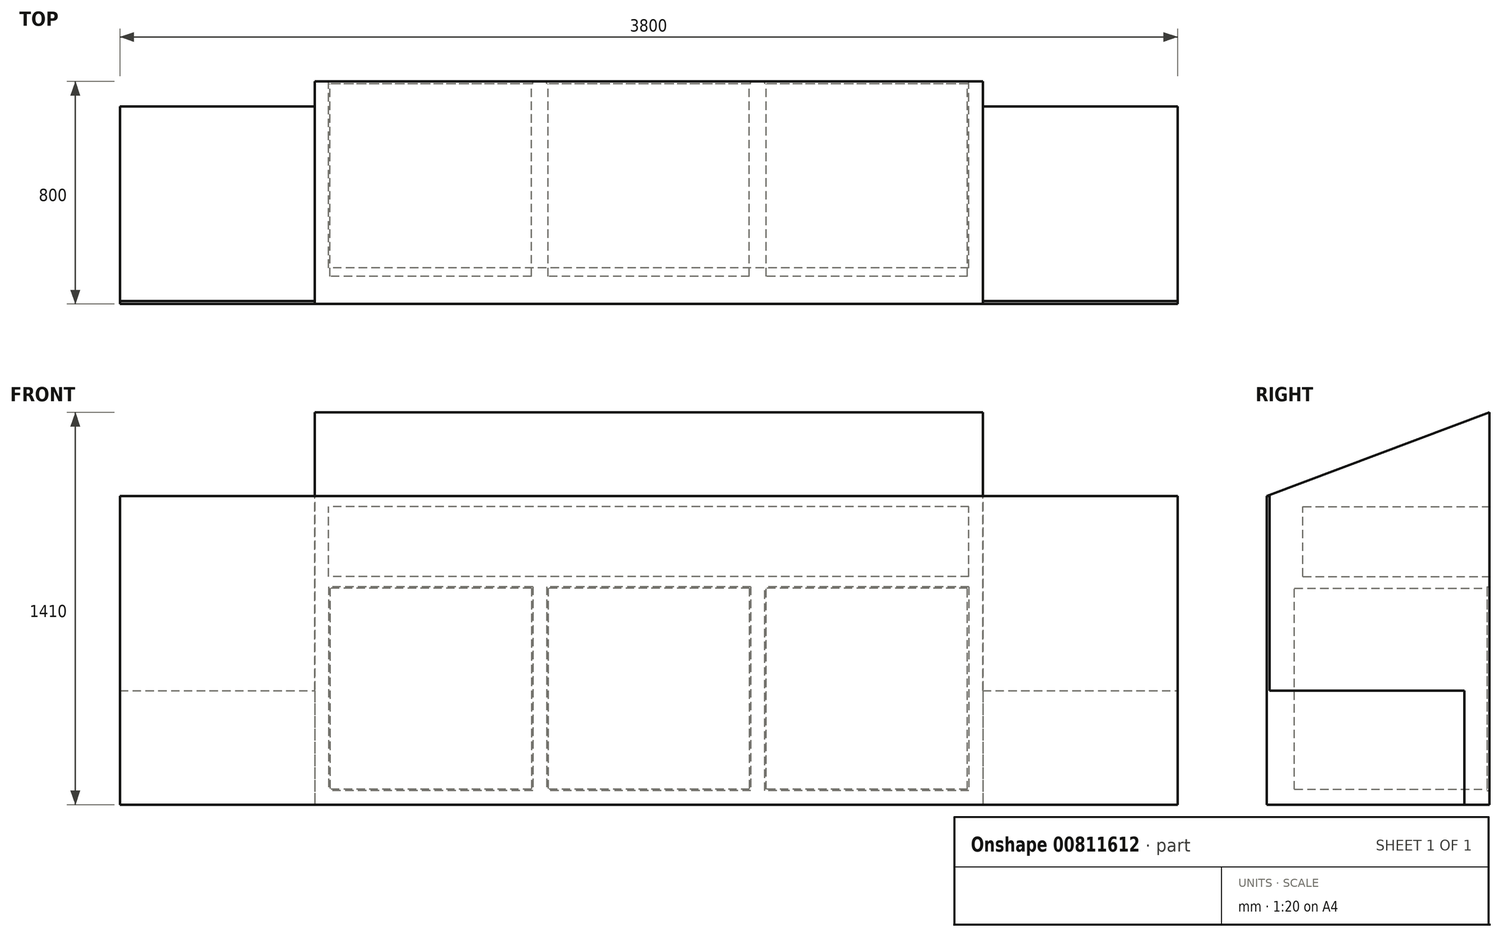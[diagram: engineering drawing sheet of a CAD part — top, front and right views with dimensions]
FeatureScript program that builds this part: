
annotation { "Feature Type Name" : "Feature", "Feature Type Description" : "" }
export const myFeature = defineFeature(function(context is Context, id is Id, definition is map)
    precondition{}
    {
        {
            var Q0;
            Q0=qCreatedBy(makeId("Top.planeOp"),FACE);
            var sketch = newSketch(context, id + "F0", { "sketchPlane" : qUnion([Q0])});
            skLineSegment(sketch, "E0.bottom", {"start": v(-1194.9, 289.22) * mm, "end": v(1205.1, 289.22) * mm});
            skLineSegment(sketch, "E0.top", {"start": v(-1194.9, -510.78) * mm, "end": v(1205.1, -510.78) * mm});
            skLineSegment(sketch, "E0.left", {"start": v(-1194.9, 289.22) * mm, "end": v(-1194.9, -510.78) * mm});
            skLineSegment(sketch, "E0.right", {"start": v(1205.1, 289.22) * mm, "end": v(1205.1, -510.78) * mm});
            skSolve(sketch);
        }
        {
            var Q0;
            Q0=makeQuery(id+"F0.imprint","IMPRINT",FACE,{"disambiguationData":[TD([[makeQuery(id+"F0.imprint","IMPRINT",EDGE,{"derivedFrom":sQuery(id+"F0.wireOp",EDGE,"E0.bottom")}),-1.0]])]});
            extrude(context, id + "F1", {"entities" : qUnion([Q0]), "depth" : 1110 * mm, "offsetDistance" : 25 * mm});
        }
        {
            var Q0;
            Q0=makeQuery(id+"F1.opExtrude","SWEPT_FACE",FACE,{"disambiguationData":[OSD([sQuery(id+"F0.wireOp",EDGE,"E0.top")])]});
            var sketch = newSketch(context, id + "F2", { "sketchPlane" : qUnion([Q0])});
            skLineSegment(sketch, "E1.bottom", {"start": v(-1194.9, 0) * mm, "end": v(-1894.9, 0) * mm});
            skLineSegment(sketch, "E1.top", {"start": v(-1194.9, 410) * mm, "end": v(-1894.9, 410) * mm});
            skLineSegment(sketch, "E1.left", {"start": v(-1194.9, 0) * mm, "end": v(-1194.9, 410) * mm});
            skLineSegment(sketch, "E1.right", {"start": v(-1894.9, 0) * mm, "end": v(-1894.9, 410) * mm});
            skLineSegment(sketch, "E2.bottom", {"start": v(1205.1, 0) * mm, "end": v(1905.1, 0) * mm});
            skLineSegment(sketch, "E2.top", {"start": v(1205.1, 410) * mm, "end": v(1905.1, 410) * mm});
            skLineSegment(sketch, "E2.left", {"start": v(1205.1, 0) * mm, "end": v(1205.1, 410) * mm});
            skLineSegment(sketch, "E2.right", {"start": v(1905.1, 0) * mm, "end": v(1905.1, 410) * mm});
            skSolve(sketch);
        }
        {
            var Q0;
            Q0 = qSketchRegion(id + "F2", true);
            extrude(context, id + "F3", {"entities" : qUnion([Q0]), "operationType" : NewBodyOperationType.ADD, "oppositeDirection" : true, "depth" : 710 * mm, "offsetDistance" : 25 * mm});
        }
        {
            var Q0;
            Q0=makeQuery(id+"F3.opExtrude","SWEPT_FACE",FACE,{"disambiguationData":[OSD([sQuery(id+"F2.wireOp",EDGE,"E2.top")])]});
            var sketch = newSketch(context, id + "F4", { "sketchPlane" : qUnion([Q0])});
            skLineSegment(sketch, "E3.0", {"start": v(-1894.9, 199.22) * mm, "end": v(-1894.9, -510.78) * mm});
            skLineSegment(sketch, "E4.bottom", {"start": v(-1894.9, -510.78) * mm, "end": v(1905.1, -510.78) * mm});
            skLineSegment(sketch, "E4.top", {"start": v(-1894.9, -500.78) * mm, "end": v(1905.1, -500.78) * mm});
            skLineSegment(sketch, "E4.left", {"start": v(-1894.9, -510.78) * mm, "end": v(-1894.9, -500.78) * mm});
            skLineSegment(sketch, "E4.right", {"start": v(1905.1, -510.78) * mm, "end": v(1905.1, -500.78) * mm});
            skSolve(sketch);
        }
        {
            var Q0;
            Q0 = qSketchRegion(id + "F4", true);
            extrude(context, id + "F5", {"entities" : qUnion([Q0]), "operationType" : NewBodyOperationType.ADD, "depth" : 700 * mm, "offsetDistance" : 25 * mm});
        }
        {
            var Q0;
            Q0=makeQuery(id+"F1.opExtrude","SWEPT_FACE",FACE,{"disambiguationData":[OSD([sQuery(id+"F0.wireOp",EDGE,"E0.left")])]});
            var sketch = newSketch(context, id + "F6", { "sketchPlane" : qUnion([Q0])});
            skLineSegment(sketch, "E5", {"start": v(-289.22, 1110) * mm, "end": v(-289.22, 1410) * mm});
            skLineSegment(sketch, "E6.0", {"start": v(-289.22, 1110) * mm, "end": v(500.78, 1110) * mm});
            skLineSegment(sketch, "E7", {"start": v(500.78, 1110) * mm, "end": v(510.78, 1110) * mm});
            skLineSegment(sketch, "E8", {"start": v(510.78, 1110) * mm, "end": v(-289.22, 1410) * mm});
            skSolve(sketch);
        }
        {
            var Q0;
            Q0=makeQuery(id+"F6.imprint","IMPRINT",FACE,{"disambiguationData":[TD([[makeQuery(id+"F6.imprint","IMPRINT",EDGE,{"derivedFrom":sQuery(id+"F6.wireOp",EDGE,"E5")}),-1.0]])]});
            var Q1;
            Q1=makeQuery(id+"F1.opExtrude","SWEPT_FACE",FACE,{"disambiguationData":[OSD([sQuery(id+"F0.wireOp",EDGE,"E0.right")])]});
            extrude(context, id + "F7", {"entities" : qUnion([Q0]), "operationType" : NewBodyOperationType.ADD, "endBound" : BoundingType.UP_TO_SURFACE, "oppositeDirection" : true, "depth" : 25 * mm, "endBoundEntityFace" : qUnion([Q1]), "offsetDistance" : 25 * mm});
        }
        {
            var Q0;
            Q0=makeQuery(id+"F7.boolean.opBoolean","MERGE",FACE,{"derivedFrom":[makeQuery(id+"F1.opExtrude","SWEPT_FACE",FACE,{"disambiguationData":[OSD([sQuery(id+"F0.wireOp",EDGE,"E0.bottom")])]}),makeQuery(id+"F7.opExtrude","SWEPT_FACE",FACE,{"disambiguationData":[OSD([sQuery(id+"F6.wireOp",EDGE,"E5")])]})]});
            var sketch = newSketch(context, id + "F8", { "sketchPlane" : qUnion([Q0])});
            skLineSegment(sketch, "E9.1", {"start": v(-1155.1, 783.3) * mm, "end": v(-1155.1, 50) * mm});
            skPoint(sketch, "E10.start.orphan", {"position": v(-1205.1, 1410) * mm});
            skPoint(sketch, "E11.end.orphan", {"position": v(1194.9, 1410) * mm});
            skLineSegment(sketch, "E12.top", {"start": v(-1155.1, 783.3) * mm, "end": v(-421.8, 783.3) * mm});
            skLineSegment(sketch, "E12.left", {"start": v(-1155.1, 50) * mm, "end": v(-1155.1, 783.3) * mm});
            skLineSegment(sketch, "E12.right", {"start": v(-421.8, 50) * mm, "end": v(-421.8, 783.3) * mm});
            skLineSegment(sketch, "E13.bottom", {"start": v(-371.8, 783.3) * mm, "end": v(361.5, 783.3) * mm});
            skLineSegment(sketch, "E13.top", {"start": v(-371.8, 50) * mm, "end": v(361.5, 50) * mm});
            skLineSegment(sketch, "E13.left", {"start": v(-371.8, 783.3) * mm, "end": v(-371.8, 50) * mm});
            skLineSegment(sketch, "E13.right", {"start": v(361.5, 783.3) * mm, "end": v(361.5, 50) * mm});
            skLineSegment(sketch, "E14.bottom", {"start": v(411.5, 783.3) * mm, "end": v(1144.8, 783.3) * mm});
            skLineSegment(sketch, "E14.top", {"start": v(411.5, 50) * mm, "end": v(1144.8, 50) * mm});
            skLineSegment(sketch, "E14.right", {"start": v(1144.8, 783.3) * mm, "end": v(1144.8, 50) * mm});
            skLineSegment(sketch, "E15.trimOffspring", {"start": v(1144.8, 50) * mm, "end": v(1144.9, 50) * mm});
            skPoint(sketch, "E16.end.orphan", {"position": v(-371.8, 627.14) * mm});
            skPoint(sketch, "E17.end.orphan", {"position": v(411.5, 495.55) * mm});
            skLineSegment(sketch, "E18", {"start": v(-1155.1, 50) * mm, "end": v(-421.8, 50) * mm});
            skLineSegment(sketch, "E19.0", {"start": v(-1150.1, 778.3) * mm, "end": v(-426.8, 778.3) * mm});
            skLineSegment(sketch, "E19.1", {"start": v(-1150.1, 55) * mm, "end": v(-1150.1, 778.3) * mm});
            skLineSegment(sketch, "E19.2", {"start": v(-1150.1, 55) * mm, "end": v(-426.8, 55) * mm});
            skLineSegment(sketch, "E19.3", {"start": v(-426.8, 55) * mm, "end": v(-426.8, 778.3) * mm});
            skLineSegment(sketch, "E20.0", {"start": v(-366.8, 778.3) * mm, "end": v(-366.8, 55) * mm});
            skLineSegment(sketch, "E20.1", {"start": v(-366.8, 778.3) * mm, "end": v(356.5, 778.3) * mm});
            skLineSegment(sketch, "E20.2", {"start": v(356.5, 778.3) * mm, "end": v(356.5, 55) * mm});
            skLineSegment(sketch, "E20.3", {"start": v(-366.8, 55) * mm, "end": v(356.5, 55) * mm});
            skLineSegment(sketch, "E21", {"start": v(411.5, 783.3) * mm, "end": v(411.5, 50) * mm});
            skLineSegment(sketch, "E22.0", {"start": v(416.5, 778.3) * mm, "end": v(1139.8, 778.3) * mm});
            skLineSegment(sketch, "E22.1", {"start": v(416.5, 778.3) * mm, "end": v(416.5, 55) * mm});
            skLineSegment(sketch, "E22.2", {"start": v(416.5, 55) * mm, "end": v(1139.8, 55) * mm});
            skLineSegment(sketch, "E22.3", {"start": v(1139.8, 778.3) * mm, "end": v(1139.8, 55) * mm});
            skSolve(sketch);
        }
        {
            var Q0;
            Q0 = qSketchRegion(id + "F8", true);
            extrude(context, id + "F9", {"entities" : qUnion([Q0]), "operationType" : NewBodyOperationType.REMOVE, "oppositeDirection" : true, "depth" : 9 * mm, "offsetDistance" : 25 * mm});
        }
        {
            var Q0;
            {var subQ1=sQuery(id+"F6.wireOp",EDGE,"E5");var subQ3=sQuery(id+"F0.wireOp",EDGE,"E0.left");var subQ4=sQuery(id+"F0.wireOp",EDGE,"E0.bottom");Q0=makeQuery(id+"F9.boolean.opBoolean","SPLIT",FACE,{"disambiguationData":[TD([makeQuery(id+"F1.opExtrude","SWEPT_FACE",FACE,{"disambiguationData":[OSD([subQ3])]})])],"derivedFrom":makeQuery(id+"F7.boolean.opBoolean","MERGE",FACE,{"derivedFrom":[makeQuery(id+"F1.opExtrude","SWEPT_FACE",FACE,{"disambiguationData":[OSD([subQ4])]}),makeQuery(id+"F7.opExtrude","SWEPT_FACE",FACE,{"disambiguationData":[OSD([subQ1])]})]})});}
            var sketch = newSketch(context, id + "F10", { "sketchPlane" : qUnion([Q0])});
            skLineSegment(sketch, "E23.bottom", {"start": v(-1155.1, 820.02) * mm, "end": v(1144.8, 820.02) * mm});
            skLineSegment(sketch, "E23.top", {"start": v(-1155.1, 1071.48) * mm, "end": v(1144.8, 1071.48) * mm});
            skLineSegment(sketch, "E23.left", {"start": v(-1155.1, 820.02) * mm, "end": v(-1155.1, 1071.48) * mm});
            skLineSegment(sketch, "E23.right", {"start": v(1144.8, 820.02) * mm, "end": v(1144.8, 1071.48) * mm});
            skSolve(sketch);
        }
        {
            var Q0;
            Q0 = qSketchRegion(id + "F10", true);
            extrude(context, id + "F11", {"entities" : qUnion([Q0]), "operationType" : NewBodyOperationType.REMOVE, "oppositeDirection" : true, "depth" : 670 * mm, "offsetDistance" : 25 * mm});
        }
        {
            var Q0;
            Q0=makeQuery(id+"F9.boolean.opBoolean","SPLIT",FACE,{"disambiguationData":[TD([makeQuery(id+"F9.opExtrude","SWEPT_FACE",FACE,{"disambiguationData":[OSD([sQuery(id+"F8.wireOp",EDGE,"E19.0")])]})])],"derivedFrom":makeQuery(id+"F7.boolean.opBoolean","MERGE",FACE,{"derivedFrom":[makeQuery(id+"F1.opExtrude","SWEPT_FACE",FACE,{"disambiguationData":[OSD([sQuery(id+"F0.wireOp",EDGE,"E0.bottom")])]}),makeQuery(id+"F7.opExtrude","SWEPT_FACE",FACE,{"disambiguationData":[OSD([sQuery(id+"F6.wireOp",EDGE,"E5")])]})]})});
            var sketch = newSketch(context, id + "F12", { "sketchPlane" : qUnion([Q0])});
            skLineSegment(sketch, "E24.0", {"start": v(-1150.1, 778.3) * mm, "end": v(-426.8, 778.3) * mm});
            skLineSegment(sketch, "E25.0", {"start": v(-1150.1, 55) * mm, "end": v(-1150.1, 778.3) * mm});
            skLineSegment(sketch, "E26.0", {"start": v(-366.8, 778.3) * mm, "end": v(356.5, 778.3) * mm});
            skLineSegment(sketch, "E27.0", {"start": v(-366.8, 778.3) * mm, "end": v(-366.8, 55) * mm});
            skLineSegment(sketch, "E28.0", {"start": v(356.5, 778.3) * mm, "end": v(356.5, 55) * mm});
            skLineSegment(sketch, "E29.0", {"start": v(-366.8, 55) * mm, "end": v(356.5, 55) * mm});
            skLineSegment(sketch, "E30.0", {"start": v(416.5, 778.3) * mm, "end": v(416.5, 55) * mm});
            skLineSegment(sketch, "E31.0", {"start": v(416.5, 55) * mm, "end": v(1139.8, 55) * mm});
            skLineSegment(sketch, "E32.0", {"start": v(1139.8, 778.3) * mm, "end": v(1139.8, 55) * mm});
            skLineSegment(sketch, "E33.0", {"start": v(416.5, 778.3) * mm, "end": v(1139.8, 778.3) * mm});
            skSolve(sketch);
        }
        {
            var Q0;
            Q0 = qSketchRegion(id + "F12", true);
            var Q1;
            Q1=makeQuery(id+"F12.imprint","IMPRINT",FACE,{"disambiguationData":[TD([[makeQuery(id+"F12.imprint","IMPRINT",EDGE,{"derivedFrom":sQuery(id+"F12.wireOp",EDGE,"E24.0")}),-1.0]])]});
            extrude(context, id + "F13", {"entities" : qUnion([Q0, Q1]), "operationType" : NewBodyOperationType.REMOVE, "oppositeDirection" : true, "depth" : 700 * mm, "offsetDistance" : 25 * mm});
        }
    });
